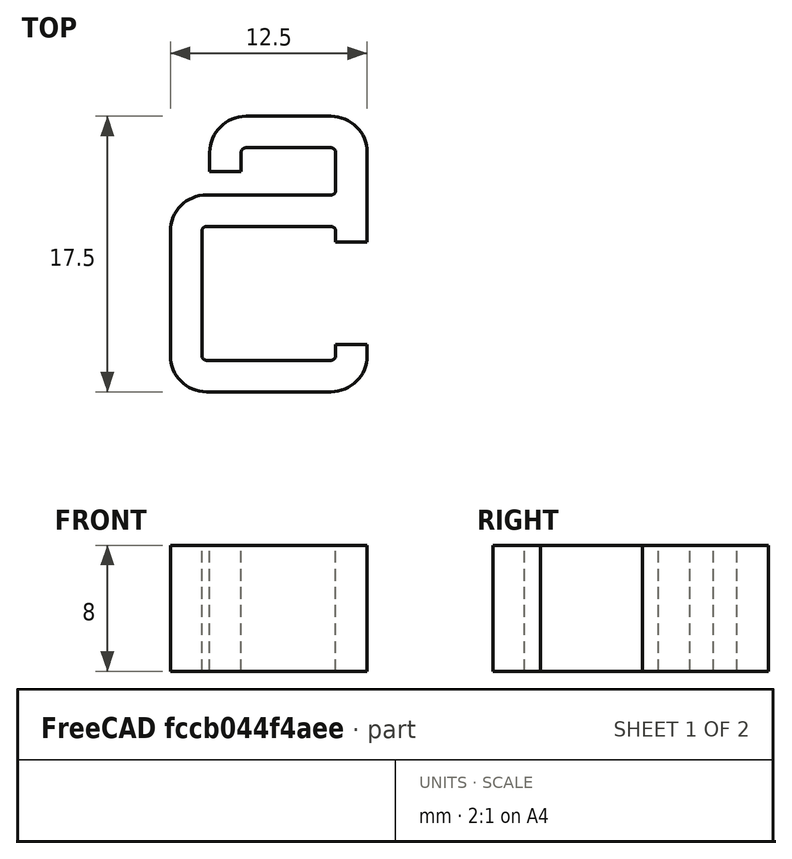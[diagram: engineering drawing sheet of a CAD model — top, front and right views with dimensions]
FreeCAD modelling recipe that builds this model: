
FCSTD DOCUMENT  (FreeCAD 1.0R39109 (Git))
Label: cable_clamp
License: All rights reserved
LicenseURL: https://en.wikipedia.org/wiki/All_rights_reserved
objects: Spreadsheet::Sheet×1, Sketcher::SketchObject×1, PartDesign::Pad×1, PartDesign::Body×1
note: 6 computed .brp shape members not serialized (recipe doc carries the construction recipe); baked Part::Feature solids carry a one-line shape summary decoded from their .brp

FEATURE [Spreadsheet::Sheet] Spreadsheet
  cells = A1='Object X; B1(obj_x_dim)=8.5; C1='Cable X; D1(cable_x)=6; A2='Object Y; B2(obj_y_dim)=8.5; C2='Cable Y; D2(cable_y)=3; A3='Object offsets; B3(obj_off)=0; C3='Gap length; D3(gap_len)=1.5; A4='Wall thickness; B4(wall_thickness)=2; A5='Inner chamfer; B5(chamfer_inner)=0.3; A6='Lip length; B6(lip_len)=1; A7='Clamp height; B7(clamp_height)=8; A9='Total Object X; B9(obj_total_x_dim)==obj_x_dim + obj_off; A10='Total Object Y; B10(obj_total_y_dim)==obj_y_dim + obj_off; A11='outer chamfer; B11(chamfer_outer)==chamfer_inner + wall_thickness
FEATURE [Sketcher::SketchObject] Sketch
  ArcFitTolerance = 1e-06
  AttachmentSupport = -> [XY_Plane]
  FullyConstrained = false
  MakeInternals = false
  MapMode = 5
  expr: Constraints[109] = Spreadsheet.gap_len
  expr: Constraints[14] = Spreadsheet.obj_total_y_dim
  expr: Constraints[15] = Spreadsheet.obj_total_x_dim
  expr: Constraints[19] = Spreadsheet.lip_len
  expr: Constraints[36] = Spreadsheet.lip_len
  expr: Constraints[55] = Spreadsheet.chamfer_inner
  expr: Constraints[64] = Spreadsheet.wall_thickness
  expr: Constraints[65] = Spreadsheet.wall_thickness
  expr: Constraints[92] = Spreadsheet.wall_thickness
  expr: Constraints[93] = Spreadsheet.wall_thickness
  expr: Constraints[94] = Spreadsheet.cable_y
  expr: Constraints[95] = Spreadsheet.cable_x
  sketch-geometry (62):
    g0: LineSegment [constr] StartX=-4.25 StartY=4.25 StartZ=0 EndX=-4.25 EndY=-4.25 EndZ=0
    g1: LineSegment [constr] StartX=-4.25 StartY=-4.25 StartZ=0 EndX=4.25 EndY=-4.25 EndZ=0
    g2: LineSegment [constr] StartX=4.25 StartY=-4.25 StartZ=0 EndX=4.25 EndY=4.25 EndZ=0
    g3: LineSegment [constr] StartX=4.25 StartY=4.25 StartZ=0 EndX=-4.25 EndY=4.25 EndZ=0
    g4: LineSegment [constr] StartX=-6.25 StartY=6.35 StartZ=0 EndX=-6.25 EndY=-6.25 EndZ=0
    g5: LineSegment [constr] StartX=-6.25 StartY=-6.25 StartZ=0 EndX=6.25 EndY=-6.25 EndZ=0
    g6: LineSegment [constr] StartX=6.25 StartY=-6.25 StartZ=0 EndX=6.25 EndY=6.25 EndZ=0
    g7: LineSegment StartX=4.25 StartY=-3.25 StartZ=0 EndX=4.25 EndY=-3.95 EndZ=0
    g8: LineSegment StartX=3.95 StartY=-4.25 StartZ=0 EndX=-3.95 EndY=-4.25 EndZ=0
    g9: ArcOfCircle CenterX=3.95 CenterY=-3.95 CenterZ=0 NormalX=0 NormalY=0 NormalZ=1 AngleXU=0 Radius=0.3 StartAngle=4.71239 EndAngle=6.28319
    g10: GeomPoint [constr] X=4.25 Y=-4.25 Z=0
    g11: LineSegment StartX=-4.25 StartY=3.95 StartZ=0 EndX=-4.25 EndY=-3.95 EndZ=0
    g12: LineSegment StartX=4.25 StartY=-3.25 StartZ=0 EndX=6.25 EndY=-3.25 EndZ=0
    g13: LineSegment StartX=6.25 StartY=-3.25 StartZ=0 EndX=6.25 EndY=-3.95 EndZ=0
    g14: LineSegment StartX=3.95 StartY=-6.25 StartZ=0 EndX=-3.95 EndY=-6.25 EndZ=0
    g15: LineSegment StartX=-6.25 StartY=-3.95 StartZ=0 EndX=-6.25 EndY=3.95 EndZ=0
    g16: LineSegment StartX=-3.95 StartY=4.25 StartZ=0 EndX=3.95 EndY=4.25 EndZ=0
    g17: LineSegment StartX=4.25 StartY=3.95 StartZ=0 EndX=4.25 EndY=3.25 EndZ=0
    g18: LineSegment StartX=6.25 StartY=6.25 StartZ=0 EndX=6.25 EndY=3.25 EndZ=0
    g19: LineSegment StartX=4.25 StartY=3.25 StartZ=0 EndX=6.25 EndY=3.25 EndZ=0
    g20: ArcOfCircle CenterX=-3.95 CenterY=-3.95 CenterZ=0 NormalX=0 NormalY=0 NormalZ=1 AngleXU=0 Radius=0.3 StartAngle=3.14159 EndAngle=4.71239
    g21: GeomPoint [constr] X=-4.25 Y=-4.25 Z=0
    g22: ArcOfCircle CenterX=-3.95 CenterY=3.95 CenterZ=0 NormalX=0 NormalY=0 NormalZ=1 AngleXU=0 Radius=0.3 StartAngle=1.5708 EndAngle=3.14159
    g23: GeomPoint [constr] X=-4.25 Y=4.25 Z=0
    g24: LineSegment [constr] StartX=-3.95 StartY=3.95 StartZ=0 EndX=-3.95 EndY=-3.95 EndZ=0
    g25: LineSegment [constr] StartX=-3.95 StartY=-3.95 StartZ=0 EndX=3.95 EndY=-3.95 EndZ=0
    g26: LineSegment [constr] StartX=3.95 StartY=-3.95 StartZ=0 EndX=3.95 EndY=3.95 EndZ=0
    g27: LineSegment [constr] StartX=3.95 StartY=3.95 StartZ=0 EndX=-3.95 EndY=3.95 EndZ=0
    g28: ArcOfCircle CenterX=3.95 CenterY=3.95 CenterZ=0 NormalX=0 NormalY=0 NormalZ=1 AngleXU=0 Radius=0.3 StartAngle=-1.8e-15 EndAngle=1.5708
    g29: GeomPoint [constr] X=4.25 Y=4.25 Z=0
    g30: ArcOfCircle CenterX=3.95 CenterY=-3.95 CenterZ=0 NormalX=0 NormalY=0 NormalZ=1 AngleXU=0 Radius=2.3 StartAngle=4.71239 EndAngle=6.28319
    g31: GeomPoint [constr] X=6.25 Y=-6.25 Z=0
    g32: ArcOfCircle CenterX=-3.95 CenterY=-3.95 CenterZ=0 NormalX=0 NormalY=0 NormalZ=1 AngleXU=0 Radius=2.3 StartAngle=3.14159 EndAngle=4.71239
    g33: GeomPoint [constr] X=-6.25 Y=-6.25 Z=0
    g34: LineSegment [constr] StartX=-3.75 StartY=11.25 StartZ=0 EndX=-3.75 EndY=6.25 EndZ=0
    g35: LineSegment [constr] StartX=-3.75 StartY=6.25 StartZ=0 EndX=6.25 EndY=6.25 EndZ=0
    g36: LineSegment [constr] StartX=6.25 StartY=6.25 StartZ=0 EndX=6.25 EndY=11.25 EndZ=0
    g37: LineSegment [constr] StartX=6.25 StartY=11.25 StartZ=0 EndX=-3.75 EndY=11.25 EndZ=0
    g38: LineSegment [constr] StartX=-1.75 StartY=9.25 StartZ=0 EndX=-1.75 EndY=6.25 EndZ=0
    g39: LineSegment [constr] StartX=-1.75 StartY=6.25 StartZ=0 EndX=4.25 EndY=6.25 EndZ=0
    g40: LineSegment [constr] StartX=4.25 StartY=6.25 StartZ=0 EndX=4.25 EndY=9.25 EndZ=0
    g41: LineSegment [constr] StartX=4.25 StartY=9.25 StartZ=0 EndX=-1.75 EndY=9.25 EndZ=0
    g42: LineSegment StartX=4.25 StartY=6.55 StartZ=0 EndX=4.25 EndY=8.95 EndZ=0
    g43: LineSegment StartX=3.95 StartY=9.25 StartZ=0 EndX=-1.45 EndY=9.25 EndZ=0
    g44: LineSegment StartX=-1.75 StartY=8.95 StartZ=0 EndX=-1.75 EndY=7.75 EndZ=0
    g45: LineSegment StartX=-3.75 StartY=8.95 StartZ=0 EndX=-3.75 EndY=7.75 EndZ=0
    g46: LineSegment StartX=-1.45 StartY=11.25 StartZ=0 EndX=3.95 EndY=11.25 EndZ=0
    g47: LineSegment StartX=6.25 StartY=8.95 StartZ=0 EndX=6.25 EndY=6.25 EndZ=0
    g48: LineSegment StartX=-3.75 StartY=7.75 StartZ=0 EndX=-1.75 EndY=7.75 EndZ=0
    g49: ArcOfCircle CenterX=-3.95 CenterY=3.95 CenterZ=0 NormalX=0 NormalY=0 NormalZ=1 AngleXU=0 Radius=2.3 StartAngle=1.5708 EndAngle=3.14159
    g50: GeomPoint [constr] X=-6.25 Y=6.35 Z=0
    g51: LineSegment StartX=-3.95 StartY=6.25 StartZ=0 EndX=3.95 EndY=6.25 EndZ=0
    g52: ArcOfCircle CenterX=-1.45 CenterY=8.95 CenterZ=0 NormalX=0 NormalY=0 NormalZ=1 AngleXU=0 Radius=0.3 StartAngle=1.5708 EndAngle=3.14159
    g53: GeomPoint [constr] X=-1.75 Y=9.25 Z=0
    g54: ArcOfCircle CenterX=3.95 CenterY=8.95 CenterZ=0 NormalX=0 NormalY=0 NormalZ=1 AngleXU=0 Radius=0.3 StartAngle=-9e-16 EndAngle=1.5708
    g55: GeomPoint [constr] X=4.25 Y=9.25 Z=0
    g56: ArcOfCircle CenterX=3.95 CenterY=6.55 CenterZ=0 NormalX=0 NormalY=0 NormalZ=1 AngleXU=0 Radius=0.3 StartAngle=4.71239 EndAngle=6.28319
    g57: GeomPoint [constr] X=4.25 Y=6.25 Z=0
    g58: ArcOfCircle CenterX=-1.45 CenterY=8.95 CenterZ=0 NormalX=0 NormalY=0 NormalZ=1 AngleXU=0 Radius=2.3 StartAngle=1.5708 EndAngle=3.14159
    g59: GeomPoint [constr] X=-3.75 Y=11.25 Z=0
    g60: ArcOfCircle CenterX=3.95 CenterY=8.95 CenterZ=0 NormalX=0 NormalY=0 NormalZ=1 AngleXU=0 Radius=2.3 StartAngle=5e-16 EndAngle=1.5708
    g61: GeomPoint [constr] X=6.25 Y=11.25 Z=0
  constraints (136):
    c: Coincident(g0,g1)
    c: Coincident(g1,g2)
    c: Coincident(g2,g3)
    c: Coincident(g3,g0)
    c: Vertical(g0)
    c: Vertical(g2)
    c: Horizontal(g1)
    c: Horizontal(g3)
    c: Coincident(g4,g5)
    c: Coincident(g5,g6)
    c: Vertical(g4)
    c: Vertical(g6)
    c: Horizontal(g5)
    c: Symmetric(g0,g1,g-1)
    c: DistanceY(g0,g0) = 8.5
    c: DistanceX(g1,g1) = 8.5
    c: Coincident(g10,g1)
    c: Coincident(g21,g0)
    c: PointOnObject(g7,g2)
    c: DistanceY(g10,g7) = 1
    c: PointOnObject(g10,g7)
    c: PointOnObject(g10,g8)
    c: Tangent(g7,g9) = 1.5708
    c: Tangent(g8,g9) = 1.5708
    c: Coincident(g23,g0)
    c: Coincident(g12,g7)
    c: PointOnObject(g12,g6)
    c: Horizontal(g12)
    c: Coincident(g13,g12)
    c: Coincident(g31,g5)
    c: Coincident(g33,g4)
    c: Coincident(g50,g4)
    c: Coincident(g29,g2)
    c: PointOnObject(g17,g2)
    c: Coincident(g18,g6)
    c: PointOnObject(g18,g6)
    c: DistanceY(g17,g2) = 1
    c: Horizontal(g18,g17)
    c: Coincident(g19,g17)
    c: Coincident(g19,g18)
    c: PointOnObject(g21,g8)
    c: PointOnObject(g21,g11)
    c: Tangent(g8,g20) = 1.5708
    c: Tangent(g11,g20) = -1.5708
    c: PointOnObject(g23,g16)
    c: Tangent(g16,g22) = 1.5708
    c: Tangent(g11,g22) = -1.5708
    c: Coincident(g24,g25)
    c: Coincident(g25,g26)
    c: Coincident(g26,g27)
    c: Coincident(g27,g24)
    c: Vertical(g24)
    c: Vertical(g26)
    c: Horizontal(g27)
    c: Symmetric(g24,g25,g-1)
    c: DistanceY(g0,g24) = 0.3
    c: Coincident(g24,g20)
    c: Coincident(g22,g24)
    c: Coincident(g9,g25)
    c: PointOnObject(g29,g17)
    c: Tangent(g17,g28) = 1.5708
    c: Tangent(g16,g28) = 1.5708
    c: Coincident(g26,g28)
    c: Symmetric(g6,g4,g-1)
    c: DistanceY(g4,g0) = 2
    c: DistanceX(g4,g0) = 2
    c: PointOnObject(g31,g13)
    c: Tangent(g13,g30) = 1.5708
    c: Tangent(g14,g30) = 1.5708
    c: Coincident(g30,g9)
    c: PointOnObject(g33,g14)
    c: Tangent(g14,g32) = 1.5708
    c: Tangent(g15,g32) = 1.5708
    c: Coincident(g32,g20)
    c: Coincident(g34,g35)
    c: Coincident(g35,g36)
    c: Coincident(g36,g37)
    c: Coincident(g37,g34)
    c: Vertical(g34)
    c: Vertical(g36)
    c: Horizontal(g35)
    c: Horizontal(g37)
    c: Coincident(g38,g39)
    c: Coincident(g39,g40)
    c: Coincident(g40,g41)
    c: Coincident(g41,g38)
    c: Vertical(g38)
    c: Vertical(g40)
    c: Horizontal(g39)
    c: Horizontal(g41)
    c: Coincident(g35,g6)
    c: Vertical(g39,g2)
    c: DistanceY(g40,g36) = 2
    c: DistanceX(g34,g38) = 2
    c: DistanceY(g39,g40) = 3
    c: DistanceX(g41,g41) = 6
    c: Coincident(g57,g39)
    c: Coincident(g55,g40)
    c: Coincident(g53,g38)
    c: PointOnObject(g44,g38)
    c: Coincident(g59,g34)
    c: PointOnObject(g45,g34)
    c: Coincident(g61,g36)
    c: Coincident(g47,g6)
    c: Coincident(g48,g45)
    c: Coincident(g48,g44)
    c: Horizontal(g48)
    c: Tangent(g15,g49) = 1.5708
    c: Coincident(g49,g22)
    c: DistanceY(g34,g45) = 1.5
    c: Tangent(g51,g49) = 1.5708
    c: Horizontal(g51)
    c: PointOnObject(g39,g35)
    c: PointOnObject(g53,g43)
    c: PointOnObject(g53,g44)
    c: Tangent(g43,g52) = -1.5708
    c: Tangent(g44,g52) = -1.5708
    c: Equal(g52,g22)
    c: PointOnObject(g55,g42)
    c: PointOnObject(g55,g43)
    c: Tangent(g42,g54) = -1.5708
    c: Tangent(g43,g54) = -1.5708
    c: Equal(g22,g54)
    c: PointOnObject(g57,g42)
    c: PointOnObject(g57,g51)
    c: Tangent(g42,g56) = -1.5708
    c: Tangent(g51,g56) = -1.5708
    c: Equal(g56,g22)
    c: PointOnObject(g59,g46)
    c: Tangent(g46,g58) = 1.5708
    c: Tangent(g45,g58) = -1.5708
    c: Coincident(g58,g52)
    c: PointOnObject(g61,g47)
    c: Tangent(g47,g60) = 1.5708
    c: Tangent(g46,g60) = 1.5708
    c: Coincident(g60,g54)
FEATURE [PartDesign::Pad] Pad  label="clamp_body"
  Direction = (0,0,1)
  Length = 8
  Length2 = 10
  Profile = -> Sketch
  ReferenceAxis = -> Sketch [N_Axis]
  Refine = true
  Suppressed = false
  Type = 0
  expr: Length = Spreadsheet.clamp_height
FEATURE [PartDesign::Body] Body
  AllowCompound = false
  Group = -> [Sketch,Pad]
  Origin = -> Origin
  Tip = -> Pad
